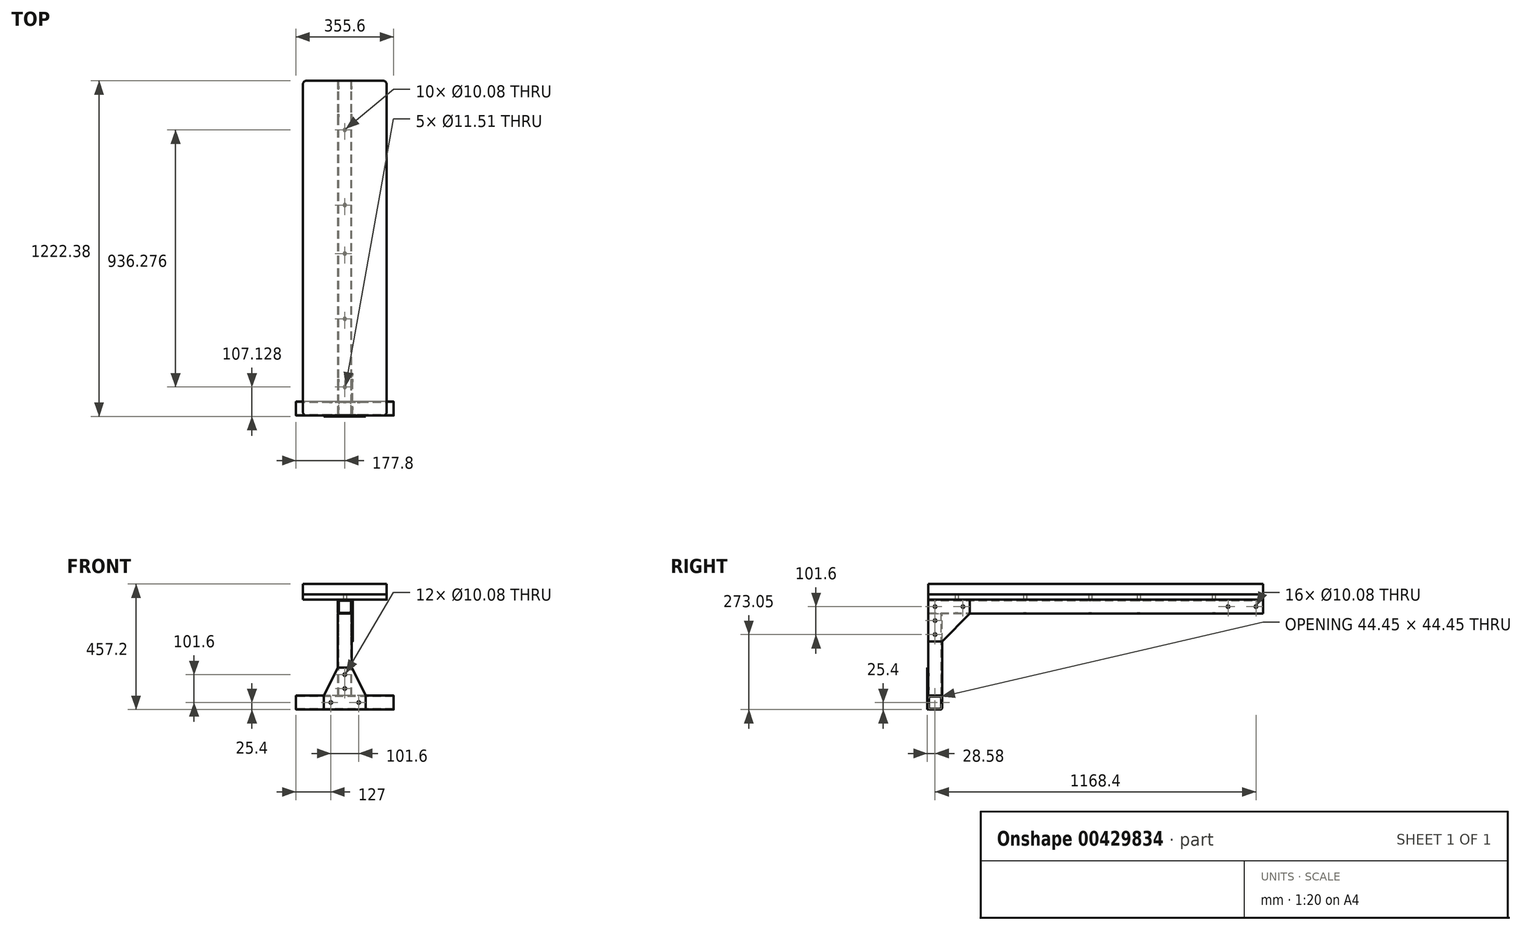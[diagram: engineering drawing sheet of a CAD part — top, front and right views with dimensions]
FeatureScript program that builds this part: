
annotation { "Feature Type Name" : "Feature", "Feature Type Description" : "" }
export const myFeature = defineFeature(function(context is Context, id is Id, definition is map)
    precondition{}
    {
        {
            var Q0;
            Q0=qCreatedBy(makeId("Right.planeOp"),FACE);
            var sketch = newSketch(context, id + "F0", { "sketchPlane" : qUnion([Q0])});
            skLineSegment(sketch, "E0", {"start": v(0, 0) * mm, "end": v(0, 3.18) * mm});
            skLineSegment(sketch, "E1", {"start": v(0, 3.17) * mm, "end": v(0, 53.98) * mm});
            skLineSegment(sketch, "E2", {"start": v(0, 0) * mm, "end": v(3.18, 0) * mm});
            skLineSegment(sketch, "E3", {"start": v(3.18, 0) * mm, "end": v(53.98, 0) * mm});
            skSolve(sketch);
        }
        {
            var Q0;
            Q0=qCreatedBy(makeId("Front.planeOp"),FACE);
            var sketch = newSketch(context, id + "F1", { "sketchPlane" : qUnion([Q0])});
            skLineSegment(sketch, "E4.bottom", {"start": v(-25.4, 0) * mm, "end": v(25.4, 0) * mm});
            skLineSegment(sketch, "E4.top", {"start": v(-25.4, -50.8) * mm, "end": v(25.4, -50.8) * mm});
            skLineSegment(sketch, "E4.left", {"start": v(-25.4, 0) * mm, "end": v(-25.4, -50.8) * mm});
            skLineSegment(sketch, "E4.right", {"start": v(25.4, 0) * mm, "end": v(25.4, -50.8) * mm});
            skLineSegment(sketch, "E5.bottom", {"start": v(-22.22, -3.18) * mm, "end": v(22.22, -3.18) * mm});
            skLineSegment(sketch, "E5.top", {"start": v(-22.22, -47.62) * mm, "end": v(22.22, -47.62) * mm});
            skLineSegment(sketch, "E5.left", {"start": v(-22.22, -3.18) * mm, "end": v(-22.22, -47.62) * mm});
            skLineSegment(sketch, "E5.right", {"start": v(22.22, -3.17) * mm, "end": v(22.22, -47.63) * mm});
            skLineSegment(sketch, "E6", {"start": v(0, -3.18) * mm, "end": v(0, 0) * mm, "construction": true});
            skLineSegment(sketch, "E7", {"start": v(0, -47.62) * mm, "end": v(0, -50.8) * mm, "construction": true});
            skLineSegment(sketch, "E8", {"start": v(22.22, -25.4) * mm, "end": v(25.4, -25.4) * mm, "construction": true});
            skSolve(sketch);
        }
        {
            var Q0;
            Q0 = qSketchRegion(id + "F1", true);
            extrude(context, id + "F2", {"entities" : qUnion([Q0]), "endBound" : BoundingType.SYMMETRIC, "depth" : 1219.2 * mm});
        }
        {
            var Q0;
            Q0=makeQuery(id+"F2.opExtrude","SWEPT_FACE",FACE,{"disambiguationData":[OSD([sQuery(id+"F1.wireOp",EDGE,"E4.top")])]});
            var sketch = newSketch(context, id + "F3", { "sketchPlane" : qUnion([Q0])});
            skLineSegment(sketch, "E9.bottom", {"start": v(25.4, 609.6) * mm, "end": v(-25.4, 609.6) * mm});
            skLineSegment(sketch, "E9.top", {"start": v(25.4, 558.8) * mm, "end": v(-25.4, 558.8) * mm});
            skLineSegment(sketch, "E9.left", {"start": v(25.4, 609.6) * mm, "end": v(25.4, 558.8) * mm});
            skLineSegment(sketch, "E9.right", {"start": v(-25.4, 609.6) * mm, "end": v(-25.4, 558.8) * mm});
            skLineSegment(sketch, "E10.bottom", {"start": v(22.22, 606.42) * mm, "end": v(-22.22, 606.42) * mm});
            skLineSegment(sketch, "E10.top", {"start": v(22.23, 561.98) * mm, "end": v(-22.22, 561.98) * mm});
            skLineSegment(sketch, "E10.left", {"start": v(22.22, 606.42) * mm, "end": v(22.22, 561.98) * mm});
            skLineSegment(sketch, "E10.right", {"start": v(-22.22, 606.42) * mm, "end": v(-22.22, 561.98) * mm});
            skLineSegment(sketch, "E11", {"start": v(0, 609.6) * mm, "end": v(0, 606.42) * mm, "construction": true});
            skLineSegment(sketch, "E12", {"start": v(22.22, 584.2) * mm, "end": v(25.4, 584.2) * mm, "construction": true});
            skLineSegment(sketch, "E13", {"start": v(-22.22, 584.2) * mm, "end": v(-25.4, 584.2) * mm, "construction": true});
            skLineSegment(sketch, "E14", {"start": v(0, 561.98) * mm, "end": v(0, 558.8) * mm, "construction": true});
            skSolve(sketch);
        }
        {
            var Q0;
            Q0 = qSketchRegion(id + "F3", true);
            extrude(context, id + "F4", {"entities" : qUnion([Q0]), "depth" : 298.45 * mm});
        }
        {
            var Q0;
            Q0=qCreatedBy(makeId("Right.planeOp"),FACE);
            var sketch = newSketch(context, id + "F5", { "sketchPlane" : qUnion([Q0])});
            skLineSegment(sketch, "E15.bottom", {"start": v(-609.6, -349.25) * mm, "end": v(-558.8, -349.25) * mm});
            skLineSegment(sketch, "E15.top", {"start": v(-609.6, -400.05) * mm, "end": v(-558.8, -400.05) * mm});
            skLineSegment(sketch, "E15.left", {"start": v(-609.6, -349.25) * mm, "end": v(-609.6, -400.05) * mm});
            skLineSegment(sketch, "E15.right", {"start": v(-558.8, -349.25) * mm, "end": v(-558.8, -400.05) * mm});
            skLineSegment(sketch, "E16.bottom", {"start": v(-606.42, -352.43) * mm, "end": v(-561.98, -352.43) * mm});
            skLineSegment(sketch, "E16.top", {"start": v(-606.42, -396.88) * mm, "end": v(-561.98, -396.88) * mm});
            skLineSegment(sketch, "E16.left", {"start": v(-606.42, -352.43) * mm, "end": v(-606.42, -396.88) * mm});
            skLineSegment(sketch, "E16.right", {"start": v(-561.98, -352.43) * mm, "end": v(-561.98, -396.88) * mm});
            skLineSegment(sketch, "E17", {"start": v(-584.2, -349.25) * mm, "end": v(-584.2, -352.43) * mm, "construction": true});
            skLineSegment(sketch, "E18", {"start": v(-609.6, -374.65) * mm, "end": v(-606.42, -374.65) * mm, "construction": true});
            skLineSegment(sketch, "E19", {"start": v(-561.98, -374.65) * mm, "end": v(-558.8, -374.65) * mm, "construction": true});
            skLineSegment(sketch, "E20", {"start": v(-584.2, -396.88) * mm, "end": v(-584.2, -400.05) * mm, "construction": true});
            skSolve(sketch);
        }
        {
            var Q0;
            Q0 = qSketchRegion(id + "F5", true);
            extrude(context, id + "F6", {"entities" : qUnion([Q0]), "endBound" : BoundingType.SYMMETRIC, "depth" : 355.6 * mm});
        }
        {
            var Q0;
            Q0=makeQuery(id+"F2.opExtrude","SWEPT_FACE",FACE,{"disambiguationData":[OSD([sQuery(id+"F1.wireOp",EDGE,"E4.right")])]});
            var sketch = newSketch(context, id + "F7", { "sketchPlane" : qUnion([Q0])});
            skLineSegment(sketch, "E21", {"start": v(-609.6, 0) * mm, "end": v(-609.6, -152.4) * mm});
            skLineSegment(sketch, "E22", {"start": v(-609.6, -152.4) * mm, "end": v(-558.8, -152.4) * mm});
            skLineSegment(sketch, "E23", {"start": v(-558.8, -152.4) * mm, "end": v(-457.2, -50.8) * mm});
            skLineSegment(sketch, "E24", {"start": v(-457.2, -50.8) * mm, "end": v(-457.2, 0) * mm});
            skLineSegment(sketch, "E25", {"start": v(-457.2, 0) * mm, "end": v(-609.6, 0) * mm});
            skSolve(sketch);
        }
        {
            var Q0;
            Q0 = qSketchRegion(id + "F7", true);
            extrude(context, id + "F8", {"entities" : qUnion([Q0]), "depth" : 3.17 * mm});
        }
        {
            var Q0;
            Q0=qCreatedBy(makeId("Top.planeOp"),FACE);
            var sketch = newSketch(context, id + "F9", { "sketchPlane" : qUnion([Q0])});
            skLineSegment(sketch, "E26.bottom", {"start": v(-152.4, -609.6) * mm, "end": v(152.4, -609.6) * mm});
            skLineSegment(sketch, "E26.top", {"start": v(-152.4, 609.6) * mm, "end": v(152.4, 609.6) * mm});
            skLineSegment(sketch, "E26.left", {"start": v(-152.4, -609.6) * mm, "end": v(-152.4, 609.6) * mm});
            skLineSegment(sketch, "E26.right", {"start": v(152.4, -609.6) * mm, "end": v(152.4, 609.6) * mm});
            skSolve(sketch);
        }
        {
            var Q0;
            Q0 = qSketchRegion(id + "F9", true);
            extrude(context, id + "F10", {"entities" : qUnion([Q0]), "depth" : 19.05 * mm});
        }
        {
            var Q0;
            Q0=makeQuery(id+"F10.opExtrude","CAP_FACE",FACE,{"disambiguationData":[OSD([sQuery(id+"F9.wireOp",EDGE,"E26.bottom"),sQuery(id+"F9.wireOp",EDGE,"E26.top"),sQuery(id+"F9.wireOp",EDGE,"E26.left"),sQuery(id+"F9.wireOp",EDGE,"E26.right")])],"isStart":false});
            extrude(context, id + "F11", {"entities" : qUnion([Q0]), "depth" : 38.1 * mm});
        }
        {
            var Q0;
            Q0=makeQuery(id+"F6.opExtrude","SWEPT_FACE",FACE,{"disambiguationData":[OSD([sQuery(id+"F5.wireOp",EDGE,"E15.left")])]});
            var sketch = newSketch(context, id + "F12", { "sketchPlane" : qUnion([Q0])});
            skLineSegment(sketch, "E27", {"start": v(-76.2, -400.05) * mm, "end": v(-76.2, -349.25) * mm});
            skLineSegment(sketch, "E28", {"start": v(-76.2, -349.25) * mm, "end": v(-25.4, -247.65) * mm});
            skLineSegment(sketch, "E29", {"start": v(-25.4, -247.65) * mm, "end": v(25.4, -247.65) * mm});
            skLineSegment(sketch, "E30", {"start": v(25.4, -247.65) * mm, "end": v(76.2, -349.25) * mm});
            skLineSegment(sketch, "E31", {"start": v(76.2, -349.25) * mm, "end": v(76.2, -400.05) * mm});
            skLineSegment(sketch, "E32", {"start": v(76.2, -400.05) * mm, "end": v(-76.2, -400.05) * mm});
            skSolve(sketch);
        }
        {
            var Q0;
            Q0 = qSketchRegion(id + "F12", true);
            extrude(context, id + "F13", {"entities" : qUnion([Q0]), "depth" : 3.17 * mm});
        }
        {
            var Q0;
            Q0=makeQuery(id+"F13.opExtrude","CAP_FACE",FACE,{"disambiguationData":[OSD([sQuery(id+"F12.wireOp",EDGE,"E27"),sQuery(id+"F12.wireOp",EDGE,"E28"),sQuery(id+"F12.wireOp",EDGE,"E29"),sQuery(id+"F12.wireOp",EDGE,"E30"),sQuery(id+"F12.wireOp",EDGE,"E31"),sQuery(id+"F12.wireOp",EDGE,"E32")])],"isStart":false});
            var sketch = newSketch(context, id + "F14", { "sketchPlane" : qUnion([Q0])});
            skPoint(sketch, "E33", {"position": v(0, -273.05) * mm});
            skPoint(sketch, "E34", {"position": v(0, -323.85) * mm});
            skPoint(sketch, "E35", {"position": v(-50.8, -374.65) * mm});
            skPoint(sketch, "E36", {"position": v(50.8, -374.65) * mm});
            skLineSegment(sketch, "E37", {"start": v(50.8, -374.65) * mm, "end": v(177.8, -374.65) * mm});
            skSolve(sketch);
        }
        {
            var Q0;
            Q0=sQuery(id+"F14.wireOp",VERTEX,"E35");
            var Q1;
            Q1=sQuery(id+"F14.wireOp",VERTEX,"E36");
            var Q2;
            Q2=sQuery(id+"F14.wireOp",VERTEX,"E34");
            var Q3;
            Q3=sQuery(id+"F14.wireOp",VERTEX,"E33");
            var Q4;
            Q4=makeQuery(id+"F6.opExtrude","SWEPT_BODY",BODY,{"disambiguationData":[OSD([sQuery(id+"F5.wireOp",EDGE,"E15.bottom"),sQuery(id+"F5.wireOp",EDGE,"E15.top"),sQuery(id+"F5.wireOp",EDGE,"E15.left"),sQuery(id+"F5.wireOp",EDGE,"E15.right"),sQuery(id+"F5.wireOp",EDGE,"E16.bottom"),sQuery(id+"F5.wireOp",EDGE,"E16.top"),sQuery(id+"F5.wireOp",EDGE,"E16.left"),sQuery(id+"F5.wireOp",EDGE,"E16.right")])]});
            var Q5;
            Q5=makeQuery(id+"F13.opExtrude","SWEPT_BODY",BODY,{"disambiguationData":[OSD([sQuery(id+"F12.wireOp",EDGE,"E27"),sQuery(id+"F12.wireOp",EDGE,"E28"),sQuery(id+"F12.wireOp",EDGE,"E29"),sQuery(id+"F12.wireOp",EDGE,"E30"),sQuery(id+"F12.wireOp",EDGE,"E31"),sQuery(id+"F12.wireOp",EDGE,"E32")])]});
            var Q6;
            Q6=makeQuery(id+"F4.opExtrude","SWEPT_BODY",BODY,{"disambiguationData":[OSD([sQuery(id+"F3.wireOp",EDGE,"E9.bottom"),sQuery(id+"F3.wireOp",EDGE,"E9.top"),sQuery(id+"F3.wireOp",EDGE,"E9.left"),sQuery(id+"F3.wireOp",EDGE,"E9.right"),sQuery(id+"F3.wireOp",EDGE,"E10.bottom"),sQuery(id+"F3.wireOp",EDGE,"E10.top"),sQuery(id+"F3.wireOp",EDGE,"E10.left"),sQuery(id+"F3.wireOp",EDGE,"E10.right")])]});
            hole(context, id + "F15", {"style" : HoleStyle.SIMPLE, "endStyle" : HoleEndStyle.THROUGH, "standardTappedOrClearance" : lookupTablePath({ "standard" : "ANSI", "fit" : "Normal (ASME)", "size" : "3/8", "type" : "Clearance" }), "standardBlindInLast" : lookupTablePath({ "fit" : "Free", "standard" : "ANSI", "size" : "3/8", "type" : "Clearance" }), "holeDiameter" : 10.08 * mm, "isTappedThrough" : true, "tappedDepth" : 12.7 * mm, "tapClearance" : 3, "locations" : qUnion([Q0, Q1, Q2, Q3]), "scope" : qUnion([Q4, Q5, Q6])});
        }
        {
            var Q0;
            Q0=makeQuery(id+"F8.opExtrude","CAP_FACE",FACE,{"disambiguationData":[OSD([sQuery(id+"F7.wireOp",EDGE,"E21"),sQuery(id+"F7.wireOp",EDGE,"E22"),sQuery(id+"F7.wireOp",EDGE,"E23"),sQuery(id+"F7.wireOp",EDGE,"E24"),sQuery(id+"F7.wireOp",EDGE,"E25")])],"isStart":false});
            var sketch = newSketch(context, id + "F16", { "sketchPlane" : qUnion([Q0])});
            skPoint(sketch, "E38", {"position": v(-482.6, -25.4) * mm});
            skPoint(sketch, "E39", {"position": v(-584.2, -25.4) * mm});
            skPoint(sketch, "E40", {"position": v(-584.2, -76.2) * mm});
            skPoint(sketch, "E41", {"position": v(-584.2, -127) * mm});
            skLineSegment(sketch, "E42", {"start": v(-584.2, -25.4) * mm, "end": v(-609.6, -25.4) * mm});
            skLineSegment(sketch, "E43", {"start": v(-584.2, -76.2) * mm, "end": v(-584.2, -50.8) * mm});
            skPoint(sketch, "E44", {"position": v(482.6, -25.4) * mm});
            skPoint(sketch, "E45", {"position": v(584.2, -25.4) * mm});
            skSolve(sketch);
        }
        {
            var Q0;
            Q0=sQuery(id+"F16.wireOp",VERTEX,"E41");
            var Q1;
            Q1=sQuery(id+"F16.wireOp",VERTEX,"E39");
            var Q2;
            Q2=sQuery(id+"F16.wireOp",VERTEX,"E40");
            var Q3;
            Q3=sQuery(id+"F16.wireOp",VERTEX,"E38");
            var Q4;
            Q4=sQuery(id+"F16.wireOp",VERTEX,"E44");
            var Q5;
            Q5=sQuery(id+"F16.wireOp",VERTEX,"E45");
            var Q6;
            Q6=makeQuery(id+"F4.opExtrude","SWEPT_BODY",BODY,{"disambiguationData":[OSD([sQuery(id+"F3.wireOp",EDGE,"E9.bottom"),sQuery(id+"F3.wireOp",EDGE,"E9.top"),sQuery(id+"F3.wireOp",EDGE,"E9.left"),sQuery(id+"F3.wireOp",EDGE,"E9.right"),sQuery(id+"F3.wireOp",EDGE,"E10.bottom"),sQuery(id+"F3.wireOp",EDGE,"E10.top"),sQuery(id+"F3.wireOp",EDGE,"E10.left"),sQuery(id+"F3.wireOp",EDGE,"E10.right")])]});
            var Q7;
            Q7=makeQuery(id+"F2.opExtrude","SWEPT_BODY",BODY,{"disambiguationData":[OSD([sQuery(id+"F1.wireOp",EDGE,"E4.bottom"),sQuery(id+"F1.wireOp",EDGE,"E4.top"),sQuery(id+"F1.wireOp",EDGE,"E4.left"),sQuery(id+"F1.wireOp",EDGE,"E4.right"),sQuery(id+"F1.wireOp",EDGE,"E5.bottom"),sQuery(id+"F1.wireOp",EDGE,"E5.top"),sQuery(id+"F1.wireOp",EDGE,"E5.left"),sQuery(id+"F1.wireOp",EDGE,"E5.right")])]});
            var Q8;
            Q8=makeQuery(id+"F8.opExtrude","SWEPT_BODY",BODY,{"disambiguationData":[OSD([sQuery(id+"F7.wireOp",EDGE,"E21"),sQuery(id+"F7.wireOp",EDGE,"E22"),sQuery(id+"F7.wireOp",EDGE,"E23"),sQuery(id+"F7.wireOp",EDGE,"E24"),sQuery(id+"F7.wireOp",EDGE,"E25")])]});
            hole(context, id + "F17", {"style" : HoleStyle.SIMPLE, "endStyle" : HoleEndStyle.THROUGH, "standardTappedOrClearance" : lookupTablePath({ "standard" : "ANSI", "fit" : "Normal (ASME)", "size" : "3/8", "type" : "Clearance" }), "standardBlindInLast" : lookupTablePath({ "fit" : "Free", "standard" : "ANSI", "size" : "3/8", "type" : "Clearance" }), "holeDiameter" : 10.08 * mm, "isTappedThrough" : true, "tappedDepth" : 12.7 * mm, "tapClearance" : 3, "locations" : qUnion([Q0, Q1, Q2, Q3, Q4, Q5]), "scope" : qUnion([Q6, Q7, Q8])});
        }
        {
            var Q0;
            Q0=qCreatedBy(makeId("Top.planeOp"),FACE);
            var sketch = newSketch(context, id + "F18", { "sketchPlane" : qUnion([Q0])});
            skPoint(sketch, "E46", {"position": v(0, -19.54) * mm});
            skPoint(sketch, "E47", {"position": v(0, -257.12) * mm});
            skPoint(sketch, "E48", {"position": v(0, -505.65) * mm});
            skPoint(sketch, "E49", {"position": v(0, 157.09) * mm});
            skPoint(sketch, "E50", {"position": v(0, 430.62) * mm});
            skSolve(sketch);
        }
        {
            var Q0;
            Q0=sQuery(id+"F18.wireOp",VERTEX,"E48");
            var Q1;
            Q1=sQuery(id+"F18.wireOp",VERTEX,"E47");
            var Q2;
            Q2=sQuery(id+"F18.wireOp",VERTEX,"E46");
            var Q3;
            Q3=sQuery(id+"F18.wireOp",VERTEX,"E49");
            var Q4;
            Q4=sQuery(id+"F18.wireOp",VERTEX,"E50");
            var Q5;
            Q5=makeQuery(id+"F2.opExtrude","SWEPT_BODY",BODY,{"disambiguationData":[OSD([sQuery(id+"F1.wireOp",EDGE,"E4.bottom"),sQuery(id+"F1.wireOp",EDGE,"E4.top"),sQuery(id+"F1.wireOp",EDGE,"E4.left"),sQuery(id+"F1.wireOp",EDGE,"E4.right"),sQuery(id+"F1.wireOp",EDGE,"E5.bottom"),sQuery(id+"F1.wireOp",EDGE,"E5.top"),sQuery(id+"F1.wireOp",EDGE,"E5.left"),sQuery(id+"F1.wireOp",EDGE,"E5.right")])]});
            hole(context, id + "F19", {"style" : HoleStyle.SIMPLE, "endStyle" : HoleEndStyle.THROUGH, "standardTappedOrClearance" : lookupTablePath({ "standard" : "ANSI", "fit" : "Normal (ASME)", "size" : "3/8", "type" : "Clearance" }), "standardBlindInLast" : lookupTablePath({ "fit" : "Free", "standard" : "ANSI", "size" : "3/8", "type" : "Clearance" }), "holeDiameter" : 10.08 * mm, "isTappedThrough" : true, "tappedDepth" : 12.7 * mm, "tapClearance" : 3, "locations" : qUnion([Q0, Q1, Q2, Q3, Q4]), "scope" : qUnion([Q5])});
        }
        {
            var Q0;
            Q0=sQuery(id+"F18.wireOp",VERTEX,"E48");
            var Q1;
            Q1=sQuery(id+"F18.wireOp",VERTEX,"E47");
            var Q2;
            Q2=sQuery(id+"F18.wireOp",VERTEX,"E46");
            var Q3;
            Q3=sQuery(id+"F18.wireOp",VERTEX,"E49");
            var Q4;
            Q4=sQuery(id+"F18.wireOp",VERTEX,"E50");
            var Q5;
            Q5=makeQuery(id+"F10.opExtrude","SWEPT_BODY",BODY,{"disambiguationData":[OSD([sQuery(id+"F9.wireOp",EDGE,"E26.bottom"),sQuery(id+"F9.wireOp",EDGE,"E26.top"),sQuery(id+"F9.wireOp",EDGE,"E26.left"),sQuery(id+"F9.wireOp",EDGE,"E26.right")])]});
            hole(context, id + "F20", {"style" : HoleStyle.SIMPLE, "endStyle" : HoleEndStyle.THROUGH, "oppositeDirection" : true, "holeDiameter" : 11.5 * mm, "isTappedThrough" : true, "tappedDepth" : 12.7 * mm, "tapClearance" : 3, "locations" : qUnion([Q0, Q1, Q2, Q3, Q4]), "scope" : qUnion([Q5])});
        }
        {
            var Q0;
            Q0=makeQuery(id+"F6.opExtrude","SWEPT_EDGE",EDGE,{"disambiguationData":[OSD([sQuery(id+"F5.wireOp",EDGE,"E15.bottom"),sQuery(id+"F5.wireOp",EDGE,"E15.left")])]});
            var Q1;
            Q1=makeQuery(id+"F6.opExtrude","SWEPT_EDGE",EDGE,{"disambiguationData":[OSD([sQuery(id+"F5.wireOp",EDGE,"E15.bottom"),sQuery(id+"F5.wireOp",EDGE,"E15.right")])]});
            var Q2;
            Q2=makeQuery(id+"F6.opExtrude","SWEPT_EDGE",EDGE,{"disambiguationData":[OSD([sQuery(id+"F5.wireOp",EDGE,"E15.top"),sQuery(id+"F5.wireOp",EDGE,"E15.right")])]});
            var Q3;
            Q3=makeQuery(id+"F6.opExtrude","SWEPT_EDGE",EDGE,{"disambiguationData":[OSD([sQuery(id+"F5.wireOp",EDGE,"E16.top"),sQuery(id+"F5.wireOp",EDGE,"E16.left")])]});
            var Q4;
            Q4=makeQuery(id+"F6.opExtrude","SWEPT_EDGE",EDGE,{"disambiguationData":[OSD([sQuery(id+"F5.wireOp",EDGE,"E15.top"),sQuery(id+"F5.wireOp",EDGE,"E15.left")])]});
            var Q5;
            Q5=makeQuery(id+"F6.opExtrude","SWEPT_EDGE",EDGE,{"disambiguationData":[OSD([sQuery(id+"F5.wireOp",EDGE,"E16.bottom"),sQuery(id+"F5.wireOp",EDGE,"E16.right")])]});
            var Q6;
            Q6=makeQuery(id+"F6.opExtrude","SWEPT_EDGE",EDGE,{"disambiguationData":[OSD([sQuery(id+"F5.wireOp",EDGE,"E16.top"),sQuery(id+"F5.wireOp",EDGE,"E16.right")])]});
            var Q7;
            Q7=makeQuery(id+"F6.opExtrude","SWEPT_EDGE",EDGE,{"disambiguationData":[OSD([sQuery(id+"F5.wireOp",EDGE,"E16.bottom"),sQuery(id+"F5.wireOp",EDGE,"E16.left")])]});
            var Q8;
            Q8=makeQuery(id+"F4.opExtrude","SWEPT_EDGE",EDGE,{"disambiguationData":[OSD([sQuery(id+"F1.wireOp",EDGE,"E4.top"),sQuery(id+"F1.wireOp",EDGE,"E4.right"),sQuery(id+"F3.wireOp",EDGE,"E9.top"),sQuery(id+"F3.wireOp",EDGE,"E9.left")])]});
            var Q9;
            Q9=makeQuery(id+"F4.opExtrude","SWEPT_EDGE",EDGE,{"disambiguationData":[OSD([sQuery(id+"F3.wireOp",EDGE,"E10.top"),sQuery(id+"F3.wireOp",EDGE,"E10.left")])]});
            var Q10;
            Q10=makeQuery(id+"F4.opExtrude","SWEPT_EDGE",EDGE,{"disambiguationData":[OSD([sQuery(id+"F3.wireOp",EDGE,"E9.bottom"),sQuery(id+"F3.wireOp",EDGE,"E9.right")])]});
            var Q11;
            Q11=makeQuery(id+"F4.opExtrude","SWEPT_EDGE",EDGE,{"disambiguationData":[OSD([sQuery(id+"F3.wireOp",EDGE,"E10.bottom"),sQuery(id+"F3.wireOp",EDGE,"E10.right")])]});
            var Q12;
            Q12=makeQuery(id+"F4.opExtrude","SWEPT_EDGE",EDGE,{"disambiguationData":[OSD([sQuery(id+"F3.wireOp",EDGE,"E9.bottom"),sQuery(id+"F3.wireOp",EDGE,"E9.left")])]});
            var Q13;
            Q13=makeQuery(id+"F4.opExtrude","SWEPT_EDGE",EDGE,{"disambiguationData":[OSD([sQuery(id+"F3.wireOp",EDGE,"E10.bottom"),sQuery(id+"F3.wireOp",EDGE,"E10.left")])]});
            var Q14;
            Q14=makeQuery(id+"F4.opExtrude","SWEPT_EDGE",EDGE,{"disambiguationData":[OSD([sQuery(id+"F3.wireOp",EDGE,"E10.top"),sQuery(id+"F3.wireOp",EDGE,"E10.right")])]});
            var Q15;
            Q15=makeQuery(id+"F4.opExtrude","SWEPT_EDGE",EDGE,{"disambiguationData":[OSD([sQuery(id+"F1.wireOp",EDGE,"E4.top"),sQuery(id+"F1.wireOp",EDGE,"E4.left"),sQuery(id+"F3.wireOp",EDGE,"E9.top"),sQuery(id+"F3.wireOp",EDGE,"E9.right")])]});
            var Q16;
            Q16=makeQuery(id+"F2.opExtrude","SWEPT_EDGE",EDGE,{"disambiguationData":[OSD([sQuery(id+"F1.wireOp",EDGE,"E4.bottom"),sQuery(id+"F1.wireOp",EDGE,"E4.right")])]});
            var Q17;
            Q17=makeQuery(id+"F2.opExtrude","SWEPT_EDGE",EDGE,{"disambiguationData":[OSD([sQuery(id+"F1.wireOp",EDGE,"E4.top"),sQuery(id+"F1.wireOp",EDGE,"E4.left")])]});
            var Q18;
            Q18=makeQuery(id+"F2.opExtrude","SWEPT_EDGE",EDGE,{"disambiguationData":[OSD([sQuery(id+"F1.wireOp",EDGE,"E4.top"),sQuery(id+"F1.wireOp",EDGE,"E4.right")])]});
            var Q19;
            Q19=makeQuery(id+"F2.opExtrude","SWEPT_EDGE",EDGE,{"disambiguationData":[OSD([sQuery(id+"F1.wireOp",EDGE,"E5.top"),sQuery(id+"F1.wireOp",EDGE,"E5.right")])]});
            var Q20;
            Q20=makeQuery(id+"F2.opExtrude","SWEPT_EDGE",EDGE,{"disambiguationData":[OSD([sQuery(id+"F1.wireOp",EDGE,"E5.bottom"),sQuery(id+"F1.wireOp",EDGE,"E5.right")])]});
            var Q21;
            Q21=makeQuery(id+"F2.opExtrude","SWEPT_EDGE",EDGE,{"disambiguationData":[OSD([sQuery(id+"F1.wireOp",EDGE,"E5.top"),sQuery(id+"F1.wireOp",EDGE,"E5.left")])]});
            var Q22;
            Q22=makeQuery(id+"F2.opExtrude","SWEPT_EDGE",EDGE,{"disambiguationData":[OSD([sQuery(id+"F1.wireOp",EDGE,"E5.bottom"),sQuery(id+"F1.wireOp",EDGE,"E5.left")])]});
            var Q23;
            Q23=makeQuery(id+"F2.opExtrude","SWEPT_EDGE",EDGE,{"disambiguationData":[OSD([sQuery(id+"F1.wireOp",EDGE,"E4.bottom"),sQuery(id+"F1.wireOp",EDGE,"E4.left")])]});
            fillet(context, id + "F21", {"entities" : qUnion([Q0, Q1, Q2, Q3, Q4, Q5, Q6, Q7, Q8, Q9, Q10, Q11, Q12, Q13, Q14, Q15, Q16, Q17, Q18, Q19, Q20, Q21, Q22, Q23]), "radius" : 5.08 * mm, "tangentPropagation" : true, "allowEdgeOverflow" : false});
        }
        {
            var Q0;
            Q0=makeQuery(id+"F11.opExtrude","SWEPT_EDGE",EDGE,{"disambiguationData":[OSD([sQuery(id+"F9.wireOp",EDGE,"E26.bottom"),sQuery(id+"F9.wireOp",EDGE,"E26.right")])]});
            var Q1;
            Q1=makeQuery(id+"F10.opExtrude","SWEPT_EDGE",EDGE,{"disambiguationData":[OSD([sQuery(id+"F9.wireOp",EDGE,"E26.bottom"),sQuery(id+"F9.wireOp",EDGE,"E26.right")])]});
            var Q2;
            Q2=makeQuery(id+"F11.opExtrude","SWEPT_EDGE",EDGE,{"disambiguationData":[OSD([sQuery(id+"F9.wireOp",EDGE,"E26.bottom"),sQuery(id+"F9.wireOp",EDGE,"E26.left")])]});
            var Q3;
            Q3=makeQuery(id+"F10.opExtrude","SWEPT_EDGE",EDGE,{"disambiguationData":[OSD([sQuery(id+"F9.wireOp",EDGE,"E26.bottom"),sQuery(id+"F9.wireOp",EDGE,"E26.left")])]});
            var Q4;
            Q4=makeQuery(id+"F11.opExtrude","SWEPT_EDGE",EDGE,{"disambiguationData":[OSD([sQuery(id+"F9.wireOp",EDGE,"E26.top"),sQuery(id+"F9.wireOp",EDGE,"E26.right")])]});
            var Q5;
            Q5=makeQuery(id+"F10.opExtrude","SWEPT_EDGE",EDGE,{"disambiguationData":[OSD([sQuery(id+"F9.wireOp",EDGE,"E26.top"),sQuery(id+"F9.wireOp",EDGE,"E26.right")])]});
            var Q6;
            Q6=makeQuery(id+"F10.opExtrude","SWEPT_EDGE",EDGE,{"disambiguationData":[OSD([sQuery(id+"F9.wireOp",EDGE,"E26.top"),sQuery(id+"F9.wireOp",EDGE,"E26.left")])]});
            var Q7;
            Q7=makeQuery(id+"F11.opExtrude","SWEPT_EDGE",EDGE,{"disambiguationData":[OSD([sQuery(id+"F9.wireOp",EDGE,"E26.top"),sQuery(id+"F9.wireOp",EDGE,"E26.left")])]});
            fillet(context, id + "F22", {"entities" : qUnion([Q0, Q1, Q2, Q3, Q4, Q5, Q6, Q7]), "radius" : 12.7 * mm, "tangentPropagation" : true, "allowEdgeOverflow" : false});
        }
        {
            var Q0;
            Q0=makeQuery(id+"F13.opExtrude","SWEPT_EDGE",EDGE,{"disambiguationData":[OSD([sQuery(id+"F5.wireOp",EDGE,"E15.bottom"),sQuery(id+"F5.wireOp",EDGE,"E15.left"),sQuery(id+"F12.wireOp",EDGE,"E30"),sQuery(id+"F12.wireOp",EDGE,"E31")])]});
            var Q1;
            Q1=makeQuery(id+"F13.opExtrude","SWEPT_EDGE",EDGE,{"disambiguationData":[OSD([sQuery(id+"F12.wireOp",EDGE,"E29"),sQuery(id+"F12.wireOp",EDGE,"E30")])]});
            var Q2;
            Q2=makeQuery(id+"F13.opExtrude","SWEPT_EDGE",EDGE,{"disambiguationData":[OSD([sQuery(id+"F12.wireOp",EDGE,"E28"),sQuery(id+"F12.wireOp",EDGE,"E29")])]});
            var Q3;
            Q3=makeQuery(id+"F13.opExtrude","SWEPT_EDGE",EDGE,{"disambiguationData":[OSD([sQuery(id+"F5.wireOp",EDGE,"E15.top"),sQuery(id+"F5.wireOp",EDGE,"E15.left"),sQuery(id+"F12.wireOp",EDGE,"E31"),sQuery(id+"F12.wireOp",EDGE,"E32")])]});
            var Q4;
            Q4=makeQuery(id+"F13.opExtrude","SWEPT_EDGE",EDGE,{"disambiguationData":[OSD([sQuery(id+"F5.wireOp",EDGE,"E15.top"),sQuery(id+"F5.wireOp",EDGE,"E15.left"),sQuery(id+"F12.wireOp",EDGE,"E27"),sQuery(id+"F12.wireOp",EDGE,"E32")])]});
            var Q5;
            Q5=makeQuery(id+"F13.opExtrude","SWEPT_EDGE",EDGE,{"disambiguationData":[OSD([sQuery(id+"F5.wireOp",EDGE,"E15.bottom"),sQuery(id+"F5.wireOp",EDGE,"E15.left"),sQuery(id+"F12.wireOp",EDGE,"E27"),sQuery(id+"F12.wireOp",EDGE,"E28")])]});
            var Q6;
            Q6=makeQuery(id+"F8.opExtrude","SWEPT_EDGE",EDGE,{"disambiguationData":[OSD([sQuery(id+"F7.wireOp",EDGE,"E21"),sQuery(id+"F7.wireOp",EDGE,"E22")])]});
            var Q7;
            Q7=makeQuery(id+"F8.opExtrude","SWEPT_EDGE",EDGE,{"disambiguationData":[OSD([sQuery(id+"F7.wireOp",EDGE,"E22"),sQuery(id+"F7.wireOp",EDGE,"E23")])]});
            var Q8;
            Q8=makeQuery(id+"F8.opExtrude","SWEPT_EDGE",EDGE,{"disambiguationData":[OSD([sQuery(id+"F7.wireOp",EDGE,"E21"),sQuery(id+"F7.wireOp",EDGE,"E25")])]});
            var Q9;
            Q9=makeQuery(id+"F8.opExtrude","SWEPT_EDGE",EDGE,{"disambiguationData":[OSD([sQuery(id+"F1.wireOp",EDGE,"E4.bottom"),sQuery(id+"F1.wireOp",EDGE,"E4.right"),sQuery(id+"F7.wireOp",EDGE,"E24"),sQuery(id+"F7.wireOp",EDGE,"E25")])]});
            var Q10;
            Q10=makeQuery(id+"F8.opExtrude","SWEPT_EDGE",EDGE,{"disambiguationData":[OSD([sQuery(id+"F1.wireOp",EDGE,"E4.top"),sQuery(id+"F1.wireOp",EDGE,"E4.right"),sQuery(id+"F7.wireOp",EDGE,"E23"),sQuery(id+"F7.wireOp",EDGE,"E24")])]});
            fillet(context, id + "F23", {"entities" : qUnion([Q0, Q1, Q2, Q3, Q4, Q5, Q6, Q7, Q8, Q9, Q10]), "radius" : 5.08 * mm, "tangentPropagation" : true, "allowEdgeOverflow" : false});
        }
    });
